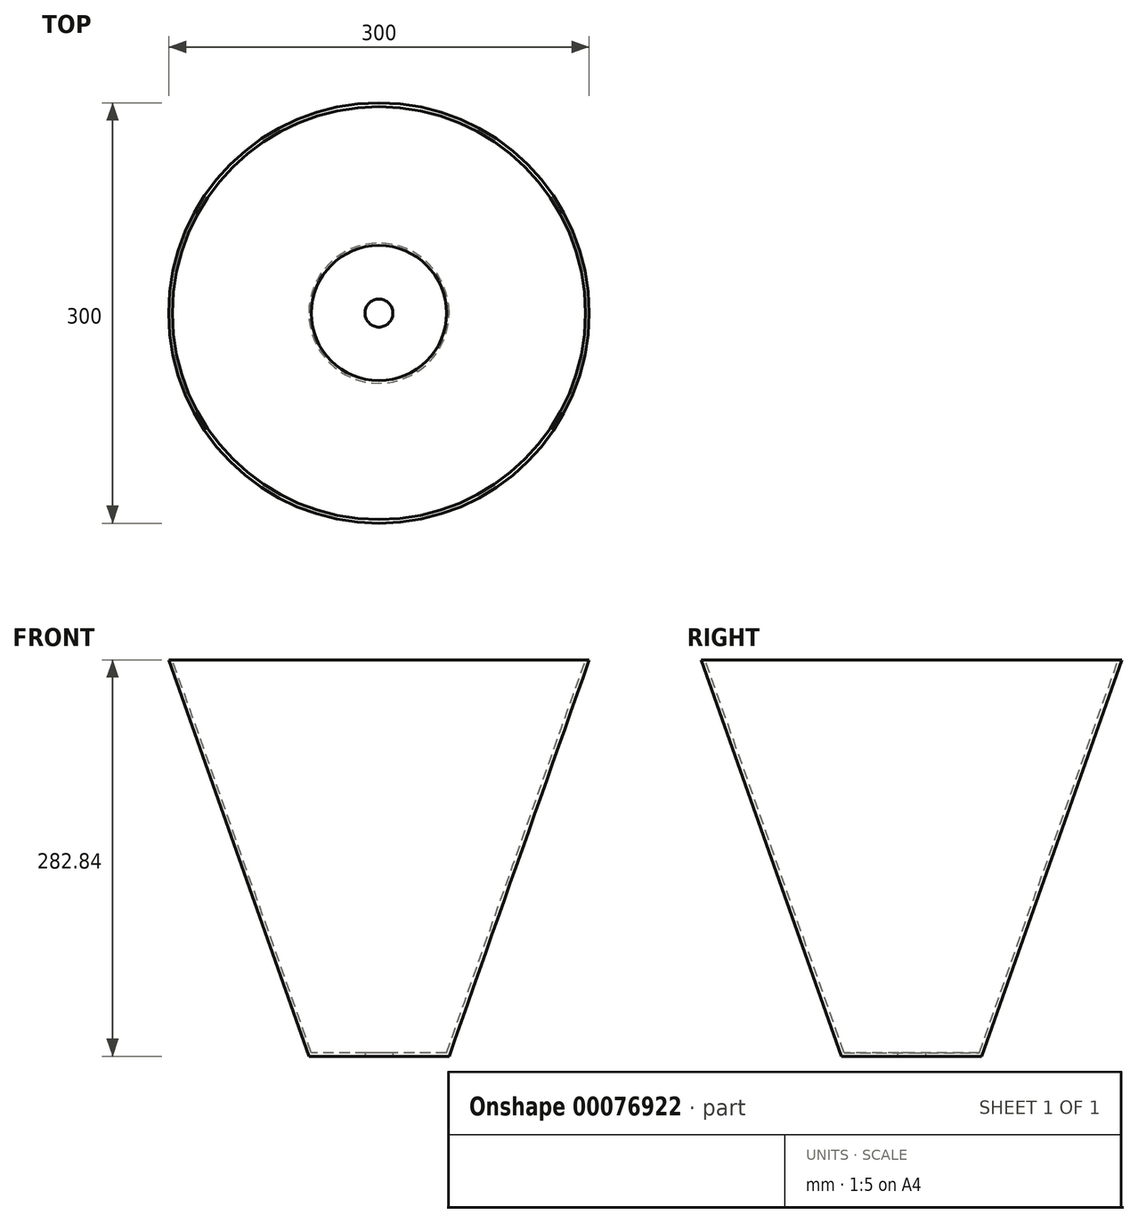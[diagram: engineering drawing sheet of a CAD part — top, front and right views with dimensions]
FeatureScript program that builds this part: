
annotation { "Feature Type Name" : "Feature", "Feature Type Description" : "" }
export const myFeature = defineFeature(function(context is Context, id is Id, definition is map)
    precondition{}
    {
        {
            var Q0;
            Q0=qCreatedBy(makeId("Right.planeOp"),FACE);
            var sketch = newSketch(context, id + "F0", { "sketchPlane" : qUnion([Q0])});
            skLineSegment(sketch, "E0", {"start": v(0, 0) * mm, "end": v(-50, 0) * mm});
            skLineSegment(sketch, "E1", {"start": v(-50, 0) * mm, "end": v(-150, 282.84) * mm});
            skLineSegment(sketch, "E2", {"start": v(-150, 282.84) * mm, "end": v(0, 282.84) * mm});
            skLineSegment(sketch, "E3", {"start": v(0, 282.84) * mm, "end": v(0, 0) * mm});
            skPoint(sketch, "E4", {"position": v(0, 0) * mm});
            skPoint(sketch, "E5", {"position": v(-25, 0) * mm});
            skSolve(sketch);
        }
        {
            var Q0;
            Q0=makeQuery(id+"F0.imprint","IMPRINT",FACE,{"disambiguationData":[TD([[makeQuery(id+"F0.imprint","IMPRINT",EDGE,{"derivedFrom":sQuery(id+"F0.wireOp",EDGE,"E0")}),-1.0]])]});
            var Q1;
            Q1=sQuery(id+"F0.wireOp",EDGE,"E3");
            revolve(context, id + "F1", {"entities" : qUnion([Q0]), "axis" : qUnion([Q1]), "revolveType" : RevolveType.FULL});
        }
        {
            var Q0;
            Q0=makeQuery(id+"F1.opRevolve","SWEPT_FACE",FACE,{"disambiguationData":[OSD([sQuery(id+"F0.wireOp",EDGE,"E2")])]});
            shell(context, id + "F2", {"entities" : qUnion([Q0]), "thickness" : 2.5 * mm});
        }
        {
            var Q0;
            Q0=makeQuery(id+"F1.opRevolve","SWEPT_FACE",FACE,{"disambiguationData":[OSD([sQuery(id+"F0.wireOp",EDGE,"E0")])]});
            var sketch = newSketch(context, id + "F3", { "sketchPlane" : qUnion([Q0])});
            skPoint(sketch, "E6", {"position": v(0, 0) * mm});
            skSolve(sketch);
        }
        {
            var Q0;
            Q0=sQuery(id+"F3.wireOp",VERTEX,"E6");
            var Q1;
            Q1=makeQuery(id+"F1.opRevolve","SWEPT_BODY",BODY,{"disambiguationData":[OSD([sQuery(id+"F0.wireOp",EDGE,"E0"),sQuery(id+"F0.wireOp",EDGE,"E1"),sQuery(id+"F0.wireOp",EDGE,"E2"),sQuery(id+"F0.wireOp",EDGE,"E3")])]});
            hole(context, id + "F4", {"style" : HoleStyle.SIMPLE, "endStyle" : HoleEndStyle.THROUGH, "holeDiameter" : 20 * mm, "locations" : qUnion([Q0]), "scope" : qUnion([Q1]), "isTappedThrough" : true});
        }
    });
